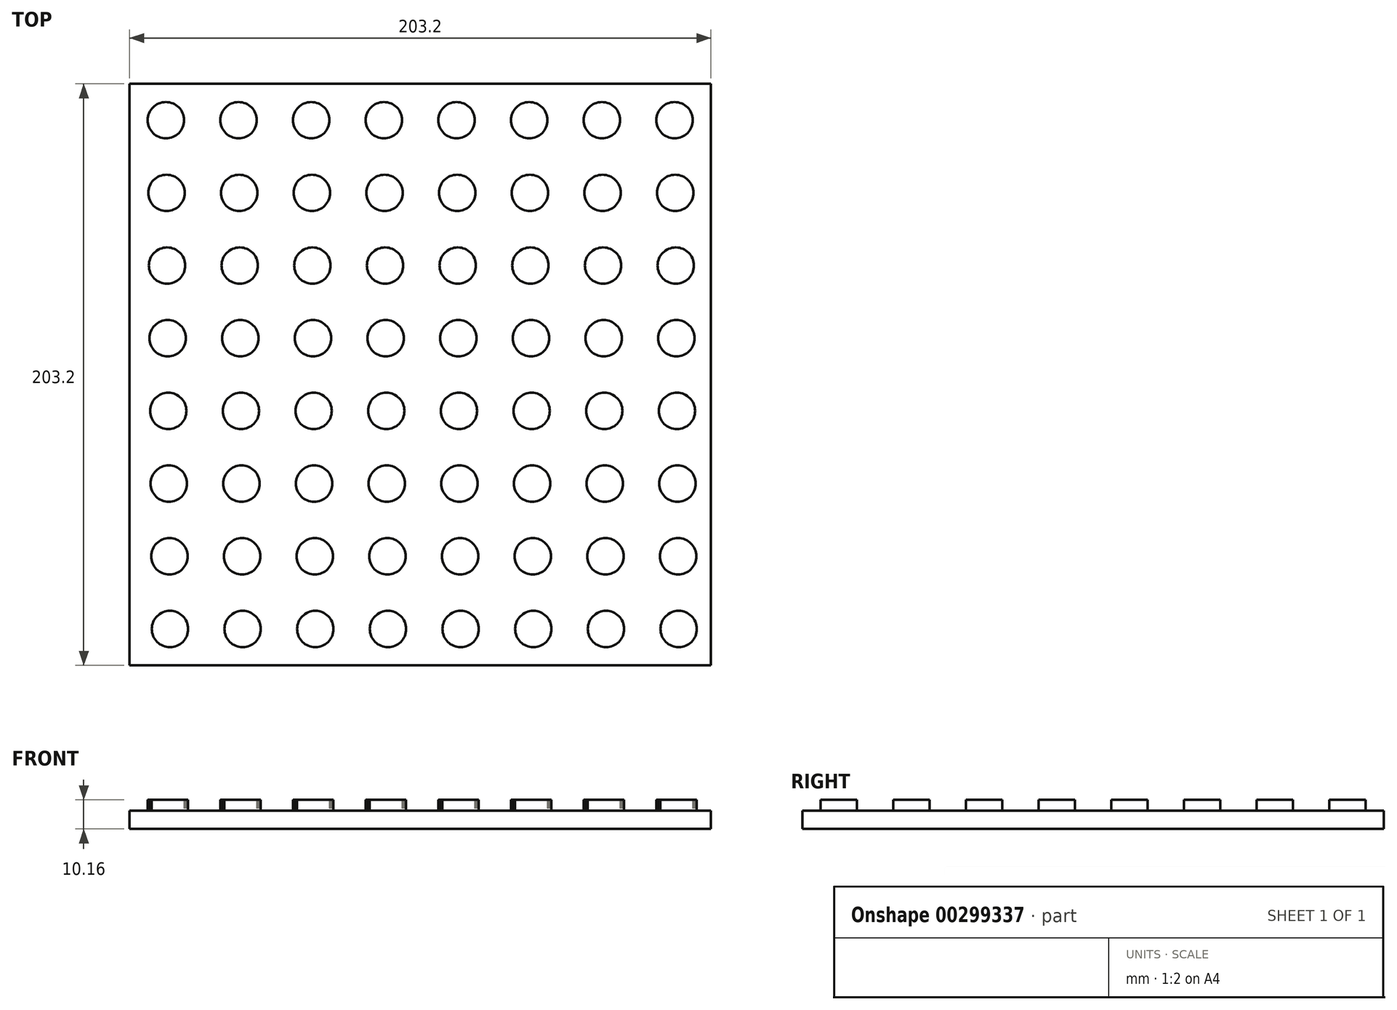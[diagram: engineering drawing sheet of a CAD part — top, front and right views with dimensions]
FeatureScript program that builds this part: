
annotation { "Feature Type Name" : "Feature", "Feature Type Description" : "" }
export const myFeature = defineFeature(function(context is Context, id is Id, definition is map)
    precondition{}
    {
        {
            var Q0;
            Q0=qCreatedBy(makeId("Top.planeOp"),FACE);
            var sketch = newSketch(context, id + "F0", { "sketchPlane" : qUnion([Q0])});
            skLineSegment(sketch, "E0.bottom", {"start": v(101.6, 101.6) * mm, "end": v(-101.6, 101.6) * mm});
            skLineSegment(sketch, "E0.top", {"start": v(101.6, -101.6) * mm, "end": v(-101.6, -101.6) * mm});
            skLineSegment(sketch, "E0.left", {"start": v(101.6, 101.6) * mm, "end": v(101.6, -101.6) * mm});
            skLineSegment(sketch, "E0.right", {"start": v(-101.6, 101.6) * mm, "end": v(-101.6, -101.6) * mm});
            skPoint(sketch, "E0.middle", {"position": v(0, 0) * mm});
            skSolve(sketch);
        }
        {
            var Q0;
            Q0 = qSketchRegion(id + "F0", true);
            extrude(context, id + "F1", {"entities" : qUnion([Q0]), "depth" : 6.35 * mm});
        }
        {
            var Q0;
            Q0=makeQuery(id+"F1.opExtrude","CAP_FACE",FACE,{"disambiguationData":[OSD([sQuery(id+"F0.wireOp",EDGE,"E0.bottom"),sQuery(id+"F0.wireOp",EDGE,"E0.top"),sQuery(id+"F0.wireOp",EDGE,"E0.left"),sQuery(id+"F0.wireOp",EDGE,"E0.right")])],"isStart":false});
            var sketch = newSketch(context, id + "F2", { "sketchPlane" : qUnion([Q0])});
            skCircle(sketch, "E1", {"center": v(-88.9, 88.9) * mm, "radius": 6.35 * mm});
            skCircle(sketch, "E2.0.1.0", {"center": v(-88.7, 63.5) * mm, "radius": 6.35 * mm});
            skCircle(sketch, "E2.0.2.0", {"center": v(-88.5, 38.1) * mm, "radius": 6.35 * mm});
            skCircle(sketch, "E2.0.3.0", {"center": v(-88.3, 12.7) * mm, "radius": 6.35 * mm});
            skCircle(sketch, "E2.0.4.0", {"center": v(-88.09, -12.7) * mm, "radius": 6.35 * mm});
            skCircle(sketch, "E2.0.5.0", {"center": v(-87.88, -38.1) * mm, "radius": 6.35 * mm});
            skCircle(sketch, "E2.0.6.0", {"center": v(-87.68, -63.5) * mm, "radius": 6.35 * mm});
            skCircle(sketch, "E2.0.7.0", {"center": v(-87.48, -88.9) * mm, "radius": 6.35 * mm});
            skCircle(sketch, "E2.1.0.0", {"center": v(-63.5, 88.9) * mm, "radius": 6.35 * mm});
            skCircle(sketch, "E2.1.1.0", {"center": v(-63.3, 63.5) * mm, "radius": 6.35 * mm});
            skCircle(sketch, "E2.1.2.0", {"center": v(-63.1, 38.1) * mm, "radius": 6.35 * mm});
            skCircle(sketch, "E2.1.3.0", {"center": v(-62.9, 12.7) * mm, "radius": 6.35 * mm});
            skCircle(sketch, "E2.1.4.0", {"center": v(-62.69, -12.7) * mm, "radius": 6.35 * mm});
            skCircle(sketch, "E2.1.5.0", {"center": v(-62.48, -38.1) * mm, "radius": 6.35 * mm});
            skCircle(sketch, "E2.1.6.0", {"center": v(-62.28, -63.5) * mm, "radius": 6.35 * mm});
            skCircle(sketch, "E2.1.7.0", {"center": v(-62.08, -88.9) * mm, "radius": 6.35 * mm});
            skCircle(sketch, "E2.2.0.0", {"center": v(-38.1, 88.9) * mm, "radius": 6.35 * mm});
            skCircle(sketch, "E2.2.1.0", {"center": v(-37.9, 63.5) * mm, "radius": 6.35 * mm});
            skCircle(sketch, "E2.2.2.0", {"center": v(-37.7, 38.1) * mm, "radius": 6.35 * mm});
            skCircle(sketch, "E2.2.3.0", {"center": v(-37.5, 12.7) * mm, "radius": 6.35 * mm});
            skCircle(sketch, "E2.2.4.0", {"center": v(-37.29, -12.7) * mm, "radius": 6.35 * mm});
            skCircle(sketch, "E2.2.5.0", {"center": v(-37.08, -38.1) * mm, "radius": 6.35 * mm});
            skCircle(sketch, "E2.2.6.0", {"center": v(-36.88, -63.5) * mm, "radius": 6.35 * mm});
            skCircle(sketch, "E2.2.7.0", {"center": v(-36.68, -88.9) * mm, "radius": 6.35 * mm});
            skCircle(sketch, "E2.3.0.0", {"center": v(-12.7, 88.9) * mm, "radius": 6.35 * mm});
            skCircle(sketch, "E2.3.1.0", {"center": v(-12.5, 63.5) * mm, "radius": 6.35 * mm});
            skCircle(sketch, "E2.3.2.0", {"center": v(-12.3, 38.1) * mm, "radius": 6.35 * mm});
            skCircle(sketch, "E2.3.3.0", {"center": v(-12.1, 12.7) * mm, "radius": 6.35 * mm});
            skCircle(sketch, "E2.3.4.0", {"center": v(-11.89, -12.7) * mm, "radius": 6.35 * mm});
            skCircle(sketch, "E2.3.5.0", {"center": v(-11.68, -38.1) * mm, "radius": 6.35 * mm});
            skCircle(sketch, "E2.3.6.0", {"center": v(-11.48, -63.5) * mm, "radius": 6.35 * mm});
            skCircle(sketch, "E2.3.7.0", {"center": v(-11.28, -88.9) * mm, "radius": 6.35 * mm});
            skCircle(sketch, "E2.4.0.0", {"center": v(12.7, 88.9) * mm, "radius": 6.35 * mm});
            skCircle(sketch, "E2.4.1.0", {"center": v(12.9, 63.5) * mm, "radius": 6.35 * mm});
            skCircle(sketch, "E2.4.2.0", {"center": v(13.1, 38.1) * mm, "radius": 6.35 * mm});
            skCircle(sketch, "E2.4.3.0", {"center": v(13.3, 12.7) * mm, "radius": 6.35 * mm});
            skCircle(sketch, "E2.4.4.0", {"center": v(13.51, -12.7) * mm, "radius": 6.35 * mm});
            skCircle(sketch, "E2.4.5.0", {"center": v(13.72, -38.1) * mm, "radius": 6.35 * mm});
            skCircle(sketch, "E2.4.6.0", {"center": v(13.92, -63.5) * mm, "radius": 6.35 * mm});
            skCircle(sketch, "E2.4.7.0", {"center": v(14.12, -88.9) * mm, "radius": 6.35 * mm});
            skCircle(sketch, "E2.5.0.0", {"center": v(38.1, 88.9) * mm, "radius": 6.35 * mm});
            skCircle(sketch, "E2.5.1.0", {"center": v(38.3, 63.5) * mm, "radius": 6.35 * mm});
            skCircle(sketch, "E2.5.2.0", {"center": v(38.5, 38.1) * mm, "radius": 6.35 * mm});
            skCircle(sketch, "E2.5.3.0", {"center": v(38.7, 12.7) * mm, "radius": 6.35 * mm});
            skCircle(sketch, "E2.5.4.0", {"center": v(38.91, -12.7) * mm, "radius": 6.35 * mm});
            skCircle(sketch, "E2.5.5.0", {"center": v(39.12, -38.1) * mm, "radius": 6.35 * mm});
            skCircle(sketch, "E2.5.6.0", {"center": v(39.32, -63.5) * mm, "radius": 6.35 * mm});
            skCircle(sketch, "E2.5.7.0", {"center": v(39.52, -88.9) * mm, "radius": 6.35 * mm});
            skCircle(sketch, "E2.6.0.0", {"center": v(63.5, 88.9) * mm, "radius": 6.35 * mm});
            skCircle(sketch, "E2.6.1.0", {"center": v(63.7, 63.5) * mm, "radius": 6.35 * mm});
            skCircle(sketch, "E2.6.2.0", {"center": v(63.9, 38.1) * mm, "radius": 6.35 * mm});
            skCircle(sketch, "E2.6.3.0", {"center": v(64.1, 12.7) * mm, "radius": 6.35 * mm});
            skCircle(sketch, "E2.6.4.0", {"center": v(64.31, -12.7) * mm, "radius": 6.35 * mm});
            skCircle(sketch, "E2.6.5.0", {"center": v(64.52, -38.1) * mm, "radius": 6.35 * mm});
            skCircle(sketch, "E2.6.6.0", {"center": v(64.72, -63.5) * mm, "radius": 6.35 * mm});
            skCircle(sketch, "E2.6.7.0", {"center": v(64.92, -88.9) * mm, "radius": 6.35 * mm});
            skCircle(sketch, "E2.7.0.0", {"center": v(88.9, 88.9) * mm, "radius": 6.35 * mm});
            skCircle(sketch, "E2.7.1.0", {"center": v(89.1, 63.5) * mm, "radius": 6.35 * mm});
            skCircle(sketch, "E2.7.2.0", {"center": v(89.3, 38.1) * mm, "radius": 6.35 * mm});
            skCircle(sketch, "E2.7.3.0", {"center": v(89.5, 12.7) * mm, "radius": 6.35 * mm});
            skCircle(sketch, "E2.7.4.0", {"center": v(89.71, -12.7) * mm, "radius": 6.35 * mm});
            skCircle(sketch, "E2.7.5.0", {"center": v(89.92, -38.1) * mm, "radius": 6.35 * mm});
            skCircle(sketch, "E2.7.6.0", {"center": v(90.12, -63.5) * mm, "radius": 6.35 * mm});
            skCircle(sketch, "E2.7.7.0", {"center": v(90.32, -88.9) * mm, "radius": 6.35 * mm});
            skLineSegment(sketch, "E2.direction1", {"start": v(-88.9, 88.9) * mm, "end": v(-63.5, 88.9) * mm, "construction": true});
            skLineSegment(sketch, "E2.direction2", {"start": v(-88.9, 88.9) * mm, "end": v(-88.7, 63.5) * mm, "construction": true});
            skSolve(sketch);
        }
        {
            var Q0;
            Q0 = qSketchRegion(id + "F2", true);
            extrude(context, id + "F3", {"entities" : qUnion([Q0]), "operationType" : NewBodyOperationType.ADD, "depth" : 3.8 * mm});
        }
    });
